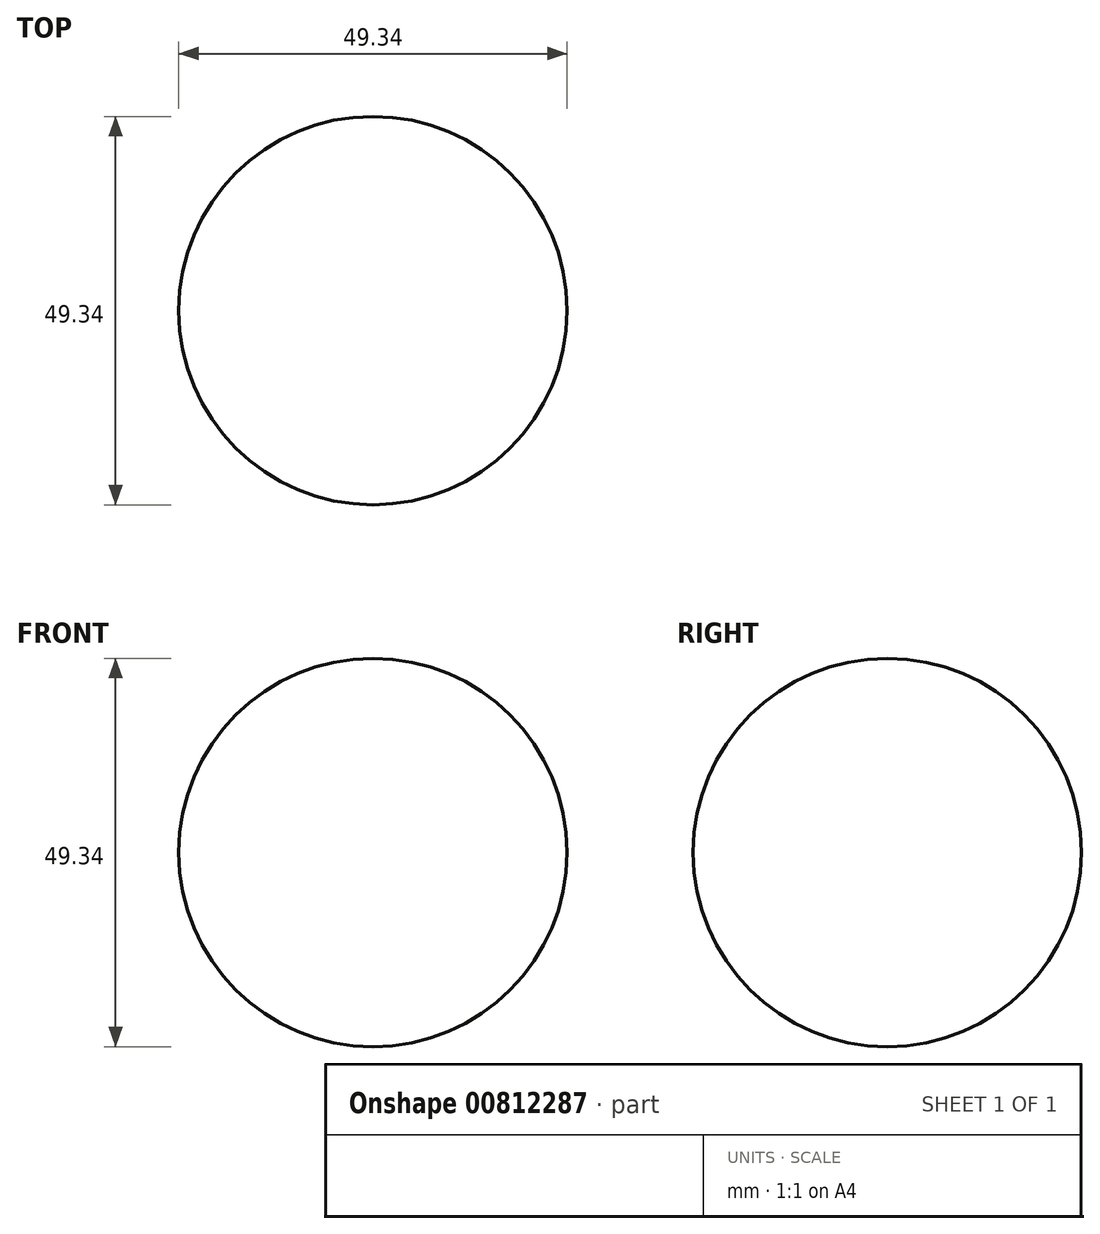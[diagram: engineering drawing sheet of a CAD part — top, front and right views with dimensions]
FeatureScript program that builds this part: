
annotation { "Feature Type Name" : "Feature", "Feature Type Description" : "" }
export const myFeature = defineFeature(function(context is Context, id is Id, definition is map)
    precondition{}
    {
        {
            var Q0;
            Q0=qCreatedBy(makeId("Front.planeOp"),FACE);
            var sketch = newSketch(context, id + "F0", { "sketchPlane" : qUnion([Q0])});
            skCircle(sketch, "E0", {"center": v(0, 0) * mm, "radius": 24.67 * mm});
            skLineSegment(sketch, "E1", {"start": v(-32.56, 0) * mm, "end": v(32.8, 0) * mm});
            skSolve(sketch);
        }
        {
            var Q0;
            {var subQ0=sQuery(id+"F0.wireOp",EDGE,"E1");var subQ1=sQuery(id+"F0.wireOp",EDGE,"E0");var subQ2=makeQuery(id+"F0.imprint","INTERSECT",VERTEX,{"disambiguationData":[OD(0.0)],"derivedFrom":[subQ1,subQ0]});Q0=makeQuery(id+"F0.imprint","IMPRINT",FACE,{"disambiguationData":[TD([[makeQuery(id+"F0.imprint","IMPRINT",EDGE,{"disambiguationData":[TD([[subQ2,-1.0]])],"derivedFrom":subQ1}),1.0]])]});}
            var Q1;
            Q1=sQuery(id+"F0.wireOp",EDGE,"E1");
            revolve(context, id + "F1", {"surfaceOperationType" : NewSurfaceOperationType.NEW, "entities" : qUnion([Q0]), "axis" : qUnion([Q1]), "revolveType" : RevolveType.FULL});
        }
    });
